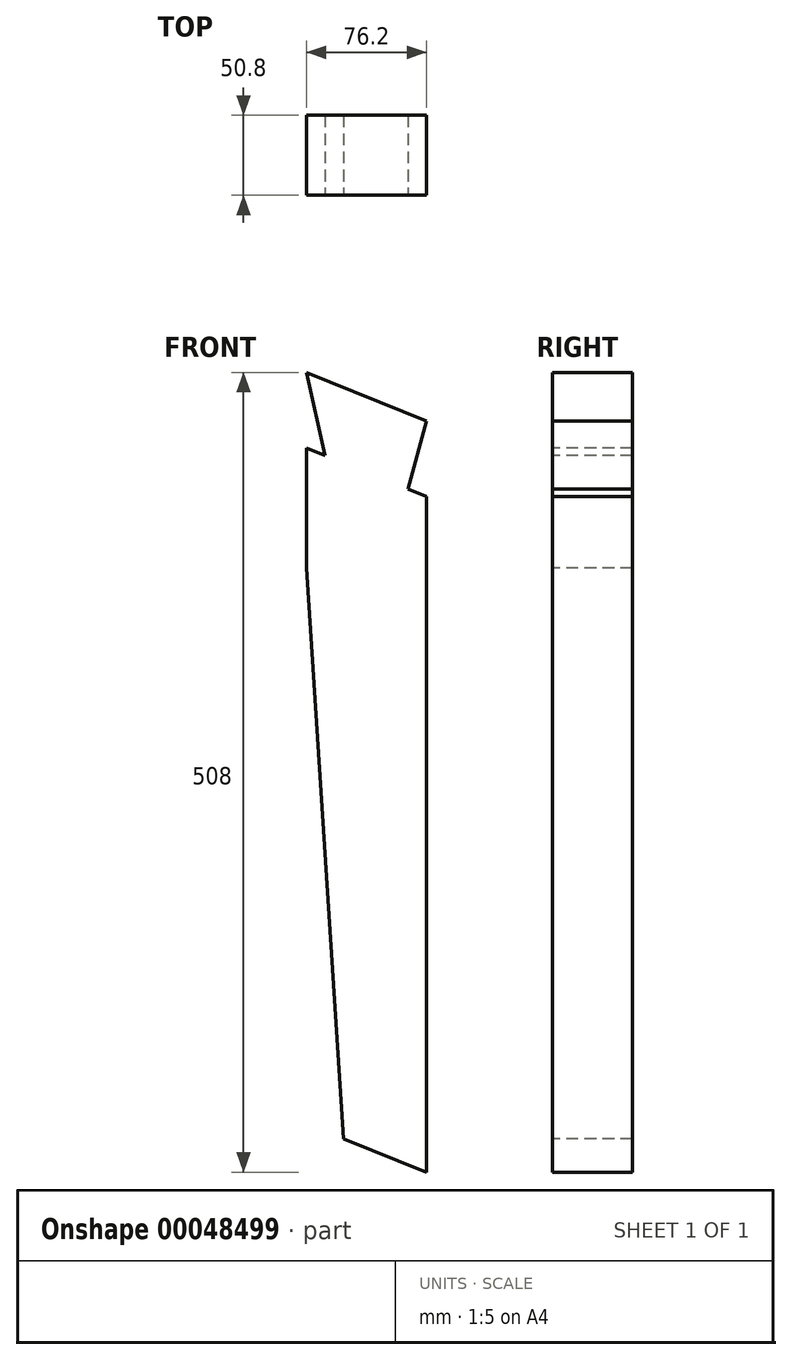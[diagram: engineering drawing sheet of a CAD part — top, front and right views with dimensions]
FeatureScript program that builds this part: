
annotation { "Feature Type Name" : "Feature", "Feature Type Description" : "" }
export const myFeature = defineFeature(function(context is Context, id is Id, definition is map)
    precondition{}
    {
        {
            var Q0;
            Q0=qCreatedBy(makeId("Front.planeOp"),FACE);
            var sketch = newSketch(context, id + "F0", { "sketchPlane" : qUnion([Q0])});
            skLineSegment(sketch, "E0.bottom", {"start": v(-38.1, 254) * mm, "end": v(38.1, 254) * mm});
            skLineSegment(sketch, "E0.top", {"start": v(-38.1, -254) * mm, "end": v(38.1, -254) * mm});
            skLineSegment(sketch, "E0.left", {"start": v(-38.1, 254) * mm, "end": v(-38.1, -254) * mm});
            skLineSegment(sketch, "E0.right", {"start": v(38.1, 254) * mm, "end": v(38.1, -254) * mm});
            skSolve(sketch);
        }
        {
            var Q0;
            Q0 = qSketchRegion(id + "F0", true);
            var Q1;
            Q1=makeQuery(id+"F0.imprint","IMPRINT",FACE,{"disambiguationData":[TD([[makeQuery(id+"F0.imprint","IMPRINT",EDGE,{"derivedFrom":sQuery(id+"F0.wireOp",EDGE,"E0.bottom")}),-1.0]])]});
            extrude(context, id + "F1", {"entities" : qUnion([Q0, Q1]), "depth" : 50.8 * mm});
        }
        {
            var Q0;
            Q0=makeQuery(id+"F1.opExtrude","CAP_FACE",FACE,{"disambiguationData":[OSD([sQuery(id+"F0.wireOp",EDGE,"E0.bottom"),sQuery(id+"F0.wireOp",EDGE,"E0.top"),sQuery(id+"F0.wireOp",EDGE,"E0.left"),sQuery(id+"F0.wireOp",EDGE,"E0.right")])],"isStart":false});
            var sketch = newSketch(context, id + "F2", { "sketchPlane" : qUnion([Q0])});
            skLineSegment(sketch, "E1.0.0", {"start": v(38.1, 254) * mm, "end": v(-38.1, 254) * mm});
            skLineSegment(sketch, "E1.0.1", {"start": v(-38.1, 254) * mm, "end": v(-38.1, -254) * mm});
            skLineSegment(sketch, "E1.0.2", {"start": v(-38.1, -254) * mm, "end": v(38.1, -254) * mm});
            skLineSegment(sketch, "E1.0.3", {"start": v(38.1, -254) * mm, "end": v(38.1, 254) * mm});
            skLineSegment(sketch, "E2", {"start": v(-38.1, 254) * mm, "end": v(38.1, 223.21) * mm});
            skLineSegment(sketch, "E3", {"start": v(-38.1, -223.21) * mm, "end": v(38.1, -254) * mm});
            skLineSegment(sketch, "E4", {"start": v(38.1, 223.21) * mm, "end": v(38.1, 254) * mm});
            skLineSegment(sketch, "E5", {"start": v(-38.1, -223.21) * mm, "end": v(-38.1, -254) * mm});
            skSolve(sketch);
        }
        {
            var Q0;
            Q0=makeQuery(id+"F2.imprint","IMPRINT",FACE,{"disambiguationData":[TD([[makeQuery(id+"F2.imprint","IMPRINT",EDGE,{"derivedFrom":sQuery(id+"F2.wireOp",EDGE,"E3")}),-1.0]])]});
            var Q1;
            Q1=makeQuery(id+"F2.imprint","IMPRINT",FACE,{"disambiguationData":[TD([[makeQuery(id+"F2.imprint","IMPRINT",EDGE,{"derivedFrom":sQuery(id+"F2.wireOp",EDGE,"E2")}),1.0]])]});
            extrude(context, id + "F3", {"entities" : qUnion([Q0, Q1]), "operationType" : NewBodyOperationType.REMOVE, "endBound" : BoundingType.THROUGH_ALL, "oppositeDirection" : true, "depth" : 25.4 * mm});
        }
        {
            var Q0;
            Q0=makeQuery(id+"F1.opExtrude","CAP_FACE",FACE,{"disambiguationData":[OSD([sQuery(id+"F0.wireOp",EDGE,"E0.bottom"),sQuery(id+"F0.wireOp",EDGE,"E0.top"),sQuery(id+"F0.wireOp",EDGE,"E0.left"),sQuery(id+"F0.wireOp",EDGE,"E0.right")])],"isStart":false});
            var sketch = newSketch(context, id + "F4", { "sketchPlane" : qUnion([Q0])});
            skLineSegment(sketch, "E6.0.0", {"start": v(-38.1, 254) * mm, "end": v(-38.1, -223.21) * mm});
            skLineSegment(sketch, "E6.0.1", {"start": v(-38.1, -223.21) * mm, "end": v(38.1, -254) * mm});
            skLineSegment(sketch, "E6.0.2", {"start": v(38.1, -254) * mm, "end": v(38.1, 223.21) * mm});
            skLineSegment(sketch, "E6.0.3", {"start": v(38.1, 223.21) * mm, "end": v(-38.1, 254) * mm});
            skLineSegment(sketch, "E7", {"start": v(-38.1, 206.06) * mm, "end": v(38.1, 175.27) * mm, "construction": true});
            skLineSegment(sketch, "E8", {"start": v(38.1, 223.21) * mm, "end": v(26.32, 180.03) * mm});
            skLineSegment(sketch, "E9", {"start": v(-38.1, 254) * mm, "end": v(-26.32, 201.3) * mm});
            skLineSegment(sketch, "E10", {"start": v(26.32, 180.03) * mm, "end": v(38.1, 175.27) * mm});
            skLineSegment(sketch, "E11", {"start": v(38.1, 175.27) * mm, "end": v(38.1, 223.21) * mm});
            skLineSegment(sketch, "E12", {"start": v(-26.32, 201.3) * mm, "end": v(-38.1, 206.06) * mm});
            skLineSegment(sketch, "E13", {"start": v(-38.1, 206.06) * mm, "end": v(-38.1, 254) * mm});
            skSolve(sketch);
        }
        {
            var Q0;
            Q0=makeQuery(id+"F4.imprint","IMPRINT",FACE,{"disambiguationData":[TD([[makeQuery(id+"F4.imprint","IMPRINT",EDGE,{"derivedFrom":sQuery(id+"F4.wireOp",EDGE,"E9")}),-1.0]])]});
            var Q1;
            Q1=makeQuery(id+"F4.imprint","IMPRINT",FACE,{"disambiguationData":[TD([[makeQuery(id+"F4.imprint","IMPRINT",EDGE,{"derivedFrom":sQuery(id+"F4.wireOp",EDGE,"E8")}),1.0]])]});
            extrude(context, id + "F5", {"entities" : qUnion([Q0, Q1]), "operationType" : NewBodyOperationType.REMOVE, "endBound" : BoundingType.THROUGH_ALL, "oppositeDirection" : true, "depth" : 25.4 * mm});
        }
        {
            var Q0;
            Q0=makeQuery(id+"F1.opExtrude","CAP_FACE",FACE,{"disambiguationData":[OSD([sQuery(id+"F0.wireOp",EDGE,"E0.bottom"),sQuery(id+"F0.wireOp",EDGE,"E0.top"),sQuery(id+"F0.wireOp",EDGE,"E0.left"),sQuery(id+"F0.wireOp",EDGE,"E0.right")])],"isStart":false});
            var sketch = newSketch(context, id + "F6", { "sketchPlane" : qUnion([Q0])});
            skLineSegment(sketch, "E14.0.0", {"start": v(38.1, 223.21) * mm, "end": v(-38.1, 254) * mm});
            skLineSegment(sketch, "E14.0.1", {"start": v(-38.1, 254) * mm, "end": v(-26.32, 201.3) * mm});
            skLineSegment(sketch, "E14.0.2", {"start": v(-26.32, 201.3) * mm, "end": v(-38.1, 206.06) * mm});
            skLineSegment(sketch, "E14.0.3", {"start": v(-38.1, 206.06) * mm, "end": v(-38.1, -223.21) * mm});
            skLineSegment(sketch, "E14.0.4", {"start": v(-38.1, -223.21) * mm, "end": v(38.1, -254) * mm});
            skLineSegment(sketch, "E14.0.5", {"start": v(38.1, -254) * mm, "end": v(38.1, 175.27) * mm});
            skLineSegment(sketch, "E14.0.6", {"start": v(38.1, 175.27) * mm, "end": v(26.32, 180.03) * mm});
            skLineSegment(sketch, "E14.0.7", {"start": v(26.32, 180.03) * mm, "end": v(38.1, 223.21) * mm});
            skLineSegment(sketch, "E15", {"start": v(-38.1, 129.86) * mm, "end": v(38.1, 99.07) * mm});
            skPoint(sketch, "E16", {"position": v(-14.55, -232.73) * mm});
            skLineSegment(sketch, "E17", {"start": v(-38.1, 129.86) * mm, "end": v(-14.55, -232.73) * mm});
            skLineSegment(sketch, "E18", {"start": v(-14.55, -232.73) * mm, "end": v(-38.1, -223.21) * mm});
            skLineSegment(sketch, "E19", {"start": v(-38.1, -223.21) * mm, "end": v(-38.1, 129.86) * mm});
            skSolve(sketch);
        }
        {
            var Q0;
            Q0=makeQuery(id+"F6.imprint","IMPRINT",FACE,{"disambiguationData":[TD([[makeQuery(id+"F6.imprint","IMPRINT",EDGE,{"derivedFrom":sQuery(id+"F6.wireOp",EDGE,"E17")}),-1.0]])]});
            extrude(context, id + "F7", {"entities" : qUnion([Q0]), "operationType" : NewBodyOperationType.REMOVE, "endBound" : BoundingType.THROUGH_ALL, "oppositeDirection" : true, "depth" : 25.4 * mm});
        }
    });
